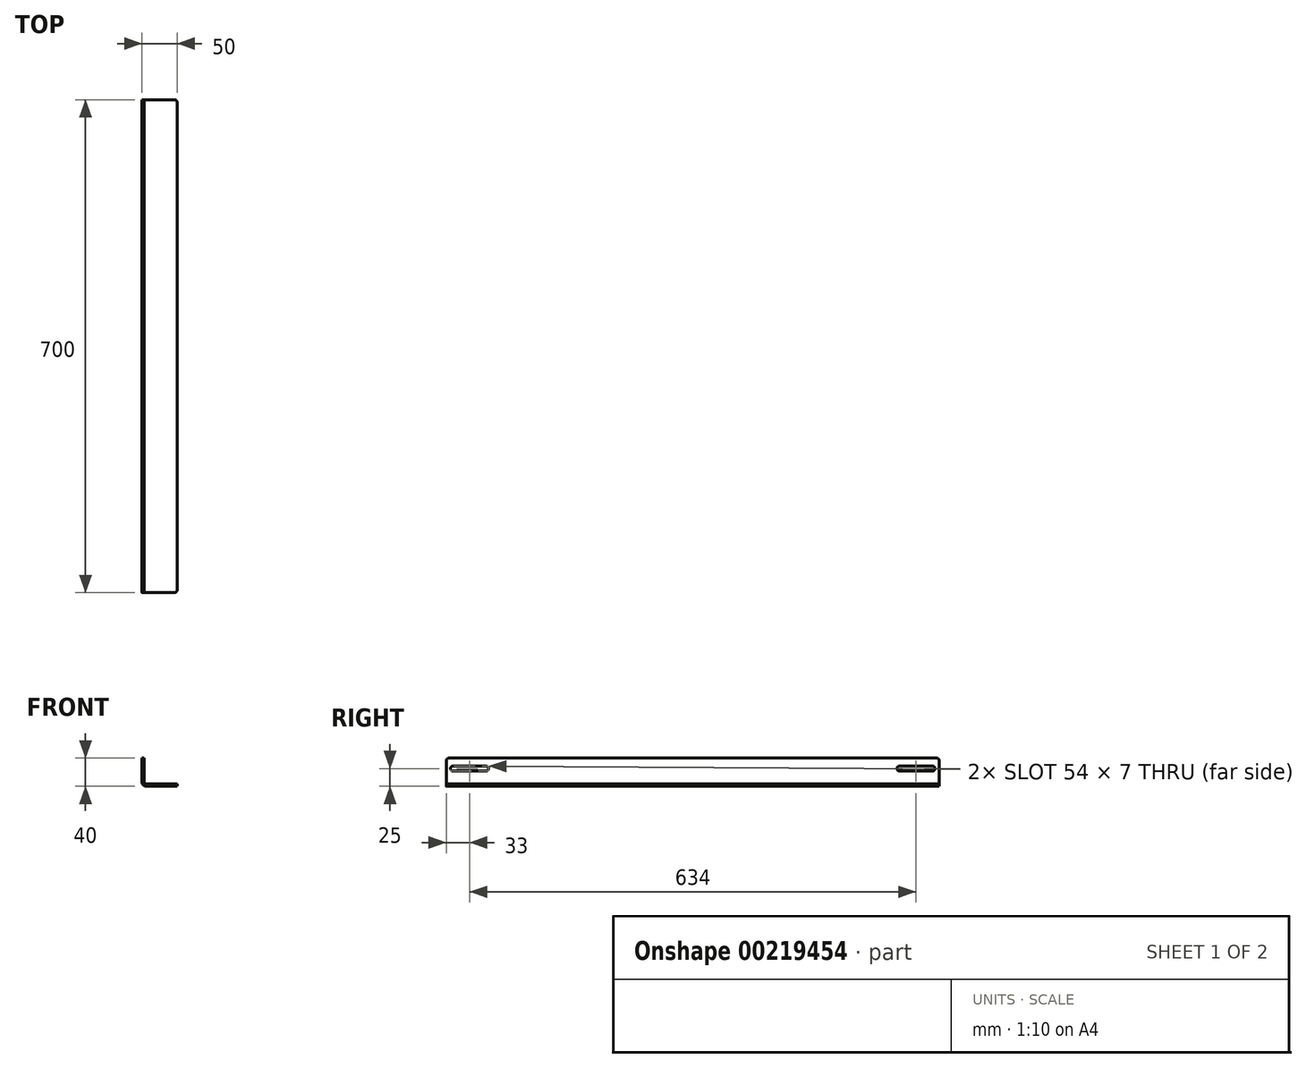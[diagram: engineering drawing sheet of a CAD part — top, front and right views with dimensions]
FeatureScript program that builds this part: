
annotation { "Feature Type Name" : "Feature", "Feature Type Description" : "" }
export const myFeature = defineFeature(function(context is Context, id is Id, definition is map)
    precondition{}
    {
        {
            var Q0;
            Q0=qCreatedBy(makeId("Front.planeOp"),FACE);
            var sketch = newSketch(context, id + "F0", { "sketchPlane" : qUnion([Q0])});
            skLineSegment(sketch, "E0.bottom", {"start": v(0, 0) * mm, "end": v(50, 0) * mm});
            skLineSegment(sketch, "E0.top", {"start": v(0, 40) * mm, "end": v(50, 40) * mm});
            skLineSegment(sketch, "E0.left", {"start": v(0, 0) * mm, "end": v(0, 40) * mm});
            skLineSegment(sketch, "E0.right", {"start": v(50, 0) * mm, "end": v(50, 40) * mm});
            skSolve(sketch);
        }
        {
            var Q0;
            Q0=makeQuery(id+"F0.imprint","IMPRINT",FACE,{"disambiguationData":[TD([[makeQuery(id+"F0.imprint","IMPRINT",EDGE,{"derivedFrom":sQuery(id+"F0.wireOp",EDGE,"E0.bottom")}),1.0]])]});
            var sketch = newSketch(context, id + "F1", { "sketchPlane" : qUnion([Q0])});
            skLineSegment(sketch, "E1.bottom", {"start": v(3, 3) * mm, "end": v(50, 3) * mm});
            skLineSegment(sketch, "E1.top", {"start": v(3, 40) * mm, "end": v(50, 40) * mm});
            skLineSegment(sketch, "E1.left", {"start": v(3, 3) * mm, "end": v(3, 40) * mm});
            skLineSegment(sketch, "E1.right", {"start": v(50, 3) * mm, "end": v(50, 40) * mm});
            skSolve(sketch);
        }
        {
            var Q0;
            Q0=makeQuery(id+"F0.imprint","IMPRINT",FACE,{"disambiguationData":[TD([[makeQuery(id+"F0.imprint","IMPRINT",EDGE,{"derivedFrom":sQuery(id+"F0.wireOp",EDGE,"E0.bottom")}),1.0]])]});
            extrude(context, id + "F2", {"entities" : qUnion([Q0]), "oppositeDirection" : true, "depth" : 700 * mm});
        }
        {
            var Q0;
            Q0=makeQuery(id+"F1.imprint","IMPRINT",FACE,{"disambiguationData":[TD([[makeQuery(id+"F1.imprint","IMPRINT",EDGE,{"derivedFrom":sQuery(id+"F1.wireOp",EDGE,"E1.bottom")}),1.0]])]});
            extrude(context, id + "F3", {"entities" : qUnion([Q0]), "operationType" : NewBodyOperationType.REMOVE, "oppositeDirection" : true, "depth" : 700 * mm});
        }
        {
            var Q0;
            Q0=makeQuery(id+"F2.opExtrude","SWEPT_EDGE",EDGE,{"disambiguationData":[OSD([sQuery(id+"F0.wireOp",EDGE,"E0.bottom"),sQuery(id+"F0.wireOp",EDGE,"E0.left")])]});
            fillet(context, id + "F4", {"entities" : qUnion([Q0]), "radius" : 6 * mm, "tangentPropagation" : true});
        }
        {
            var Q0;
            Q0=makeQuery(id+"F3.boolean.opBoolean","COPY",EDGE,{"derivedFrom":makeQuery(id+"F3.opExtrude","SWEPT_EDGE",EDGE,{"disambiguationData":[OSD([sQuery(id+"F1.wireOp",EDGE,"E1.bottom"),sQuery(id+"F1.wireOp",EDGE,"E1.left")])]})});
            fillet(context, id + "F5", {"entities" : qUnion([Q0]), "radius" : 3 * mm, "tangentPropagation" : true});
        }
        {
            var Q0;
            Q0=makeQuery(id+"F2.opExtrude","CAP_EDGE",EDGE,{"disambiguationData":[OSD([sQuery(id+"F0.wireOp",EDGE,"E0.top")])],"isStart":true});
            fillet(context, id + "F6", {"entities" : qUnion([Q0]), "radius" : 4 * mm, "tangentPropagation" : true});
        }
        {
            var Q0;
            Q0=makeQuery(id+"F2.opExtrude","CAP_EDGE",EDGE,{"disambiguationData":[OSD([sQuery(id+"F0.wireOp",EDGE,"E0.top")])],"isStart":false});
            fillet(context, id + "F7", {"entities" : qUnion([Q0]), "radius" : 4 * mm, "tangentPropagation" : true});
        }
        {
            var Q0;
            Q0=makeQuery(id+"F2.opExtrude","CAP_EDGE",EDGE,{"disambiguationData":[OSD([sQuery(id+"F0.wireOp",EDGE,"E0.right")])],"isStart":true});
            fillet(context, id + "F8", {"entities" : qUnion([Q0]), "radius" : 4 * mm, "tangentPropagation" : true});
        }
        {
            var Q0;
            Q0=makeQuery(id+"F2.opExtrude","CAP_EDGE",EDGE,{"disambiguationData":[OSD([sQuery(id+"F0.wireOp",EDGE,"E0.right")])],"isStart":false});
            fillet(context, id + "F9", {"entities" : qUnion([Q0]), "radius" : 4 * mm, "tangentPropagation" : true});
        }
        {
            var Q0;
            Q0=makeQuery(id+"F2.opExtrude","SWEPT_FACE",FACE,{"disambiguationData":[OSD([sQuery(id+"F0.wireOp",EDGE,"E0.left")])]});
            var sketch = newSketch(context, id + "F10", { "sketchPlane" : qUnion([Q0])});
            skLineSegment(sketch, "E2.bottom", {"start": v(-690.5, 28.5) * mm, "end": v(-643.5, 28.5) * mm});
            skLineSegment(sketch, "E2.top", {"start": v(-690.5, 21.5) * mm, "end": v(-643.5, 21.5) * mm});
            skLineSegment(sketch, "E2.left", {"start": v(-690.5, 28.5) * mm, "end": v(-690.5, 21.5) * mm});
            skLineSegment(sketch, "E2.right", {"start": v(-643.5, 28.5) * mm, "end": v(-643.5, 21.5) * mm});
            skArc(sketch, "E3", {"start": v(-690.5, 28.5) * mm, "mid": v(-694, 25) * mm, "end": v(-690.5, 21.5) * mm});
            skArc(sketch, "E4", {"start": v(-643.5, 21.5) * mm, "mid": v(-640, 25) * mm, "end": v(-643.5, 28.5) * mm});
            skSolve(sketch);
        }
        {
            var Q0;
            Q0=makeQuery(id+"F10.imprint","IMPRINT",FACE,{"disambiguationData":[TD([[makeQuery(id+"F10.imprint","IMPRINT",EDGE,{"derivedFrom":sQuery(id+"F10.wireOp",EDGE,"E2.bottom")}),-1.0]])]});
            var Q1;
            Q1=makeQuery(id+"F10.imprint","IMPRINT",FACE,{"disambiguationData":[TD([[makeQuery(id+"F10.imprint","IMPRINT",EDGE,{"derivedFrom":sQuery(id+"F10.wireOp",EDGE,"E2.left")}),-1.0]])]});
            var Q2;
            Q2=makeQuery(id+"F10.imprint","IMPRINT",FACE,{"disambiguationData":[TD([[makeQuery(id+"F10.imprint","IMPRINT",EDGE,{"derivedFrom":sQuery(id+"F10.wireOp",EDGE,"E2.right")}),1.0]])]});
            extrude(context, id + "F11", {"entities" : qUnion([Q0, Q1, Q2]), "operationType" : NewBodyOperationType.REMOVE, "oppositeDirection" : true, "depth" : 3 * mm});
        }
        {
            var Q0;
            Q0=makeQuery(id+"F2.opExtrude","SWEPT_FACE",FACE,{"disambiguationData":[OSD([sQuery(id+"F0.wireOp",EDGE,"E0.left")])]});
            var sketch = newSketch(context, id + "F12", { "sketchPlane" : qUnion([Q0])});
            skLineSegment(sketch, "E5.bottom", {"start": v(-56.5, 28.5) * mm, "end": v(-9.5, 28.5) * mm});
            skLineSegment(sketch, "E5.top", {"start": v(-56.5, 21.5) * mm, "end": v(-9.5, 21.5) * mm});
            skLineSegment(sketch, "E5.left", {"start": v(-56.5, 28.5) * mm, "end": v(-56.5, 21.5) * mm});
            skLineSegment(sketch, "E5.right", {"start": v(-9.5, 28.5) * mm, "end": v(-9.5, 21.5) * mm});
            skArc(sketch, "E6", {"start": v(-56.5, 28.5) * mm, "mid": v(-60, 25) * mm, "end": v(-56.5, 21.5) * mm});
            skArc(sketch, "E7", {"start": v(-9.5, 21.5) * mm, "mid": v(-6, 25) * mm, "end": v(-9.5, 28.5) * mm});
            skSolve(sketch);
        }
        {
            var Q0;
            Q0=qSketchRegion(id+"F12",true);
            var Q1;
            Q1=makeQuery(id+"F12.imprint","IMPRINT",FACE,{"disambiguationData":[TD([[makeQuery(id+"F12.imprint","IMPRINT",EDGE,{"derivedFrom":sQuery(id+"F12.wireOp",EDGE,"E5.bottom")}),-1.0]])]});
            extrude(context, id + "F13", {"entities" : qUnion([Q0, Q1]), "operationType" : NewBodyOperationType.REMOVE, "oppositeDirection" : true, "depth" : 3 * mm});
        }
    });
